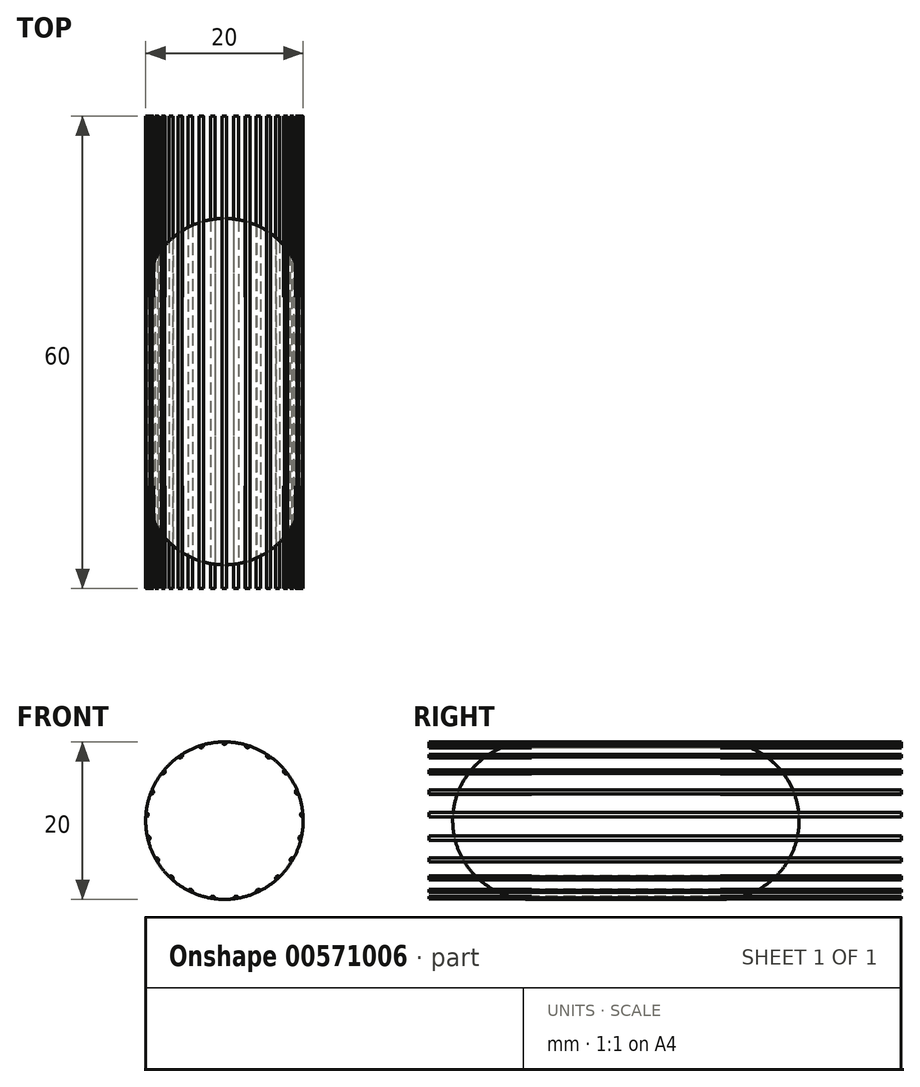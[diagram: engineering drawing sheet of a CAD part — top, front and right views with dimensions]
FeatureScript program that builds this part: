
annotation { "Feature Type Name" : "Feature", "Feature Type Description" : "" }
export const myFeature = defineFeature(function(context is Context, id is Id, definition is map)
    precondition{}
    {
        {
            var Q0;
            Q0=qCreatedBy(makeId("Right.planeOp"),FACE);
            var sketch = newSketch(context, id + "F0", { "sketchPlane" : qUnion([Q0])});
            skPoint(sketch, "E0", {"position": v(-22, 0) * mm});
            skPoint(sketch, "E1", {"position": v(-12, 0) * mm});
            skPoint(sketch, "E2", {"position": v(-12, 10) * mm});
            skEllipse(sketch, "E3", {"center": v(-12, 0) * mm, "majorRadius": 10 * mm, "minorRadius": 10 * mm, "majorAxis": v(-1, 0)});
            skLineSegment(sketch, "E4", {"start": v(-12, 10) * mm, "end": v(0, 10) * mm});
            skLineSegment(sketch, "E5", {"start": v(0, 10) * mm, "end": v(0, 0) * mm});
            skLineSegment(sketch, "E6", {"start": v(0, 0) * mm, "end": v(0, -10) * mm});
            skPoint(sketch, "E6.endSnap0", {"position": v(-12, -10) * mm});
            skLineSegment(sketch, "E7", {"start": v(0, -10) * mm, "end": v(-12, -10) * mm});
            skPoint(sketch, "E8.MirrorP", {"position": v(12, -10) * mm});
            skPoint(sketch, "E9.MirrorP", {"position": v(12, 10) * mm});
            skPoint(sketch, "E10.MirrorP", {"position": v(12, 0) * mm});
            skEllipse(sketch, "E11.MirrorC", {"center": v(12, 0) * mm, "majorRadius": 10 * mm, "minorRadius": 10 * mm, "majorAxis": v(1, 0)});
            skLineSegment(sketch, "E12.MirrorCS", {"start": v(12, 10) * mm, "end": v(0, 10) * mm});
            skPoint(sketch, "E13.MirrorP", {"position": v(22, 0) * mm});
            skLineSegment(sketch, "E14.MirrorCS", {"start": v(0, -10) * mm, "end": v(12, -10) * mm});
            skLineSegment(sketch, "E15", {"start": v(-12, 0) * mm, "end": v(12, 0) * mm});
            skLineSegment(sketch, "E16", {"start": v(-12, 0) * mm, "end": v(-22, 0) * mm});
            skLineSegment(sketch, "E17", {"start": v(12, 0) * mm, "end": v(22, 0) * mm});
            skSolve(sketch);
        }
        {
            var Q0;
            {var subQ4=sQuery(id+"F0.wireOp",EDGE,"E16");Q0=makeQuery(id+"F0.imprint","IMPRINT",FACE,{"disambiguationData":[TD([[makeQuery(id+"F0.imprint","IMPRINT",EDGE,{"derivedFrom":subQ4}),-1.0]])]});}
            var Q1;
            {var subQ0=sQuery(id+"F0.wireOp",EDGE,"E4");Q1=makeQuery(id+"F0.imprint","IMPRINT",FACE,{"disambiguationData":[TD([[makeQuery(id+"F0.imprint","IMPRINT",EDGE,{"derivedFrom":subQ0}),-1.0]])]});}
            var Q2;
            {var subQ0=sQuery(id+"F0.wireOp",EDGE,"E5");Q2=makeQuery(id+"F0.imprint","IMPRINT",FACE,{"disambiguationData":[TD([[makeQuery(id+"F0.imprint","IMPRINT",EDGE,{"derivedFrom":subQ0}),1.0]])]});}
            var Q3;
            {var subQ2=sQuery(id+"F0.wireOp",EDGE,"E17");Q3=makeQuery(id+"F0.imprint","IMPRINT",FACE,{"disambiguationData":[TD([[makeQuery(id+"F0.imprint","IMPRINT",EDGE,{"derivedFrom":subQ2}),1.0]])]});}
            var Q4;
            Q4=sQuery(id+"F0.wireOp",EDGE,"E15");
            revolve(context, id + "F1", {"entities" : qUnion([Q0, Q1, Q2, Q3]), "axis" : qUnion([Q4]), "revolveType" : RevolveType.FULL});
        }
        {
            var Q0;
            Q0=qCreatedBy(makeId("Front.planeOp"),FACE);
            cPlane(context, id + "F2", {"entities" : qUnion([Q0]), "cplaneType" : CPlaneType.OFFSET, "offset" : 25 * mm, "width" : 150 * mm, "height" : 150 * mm});
        }
        {
            var Q0;
            Q0=qCreatedBy(id+"F2.planeOp",FACE);
            var sketch = newSketch(context, id + "F3", { "sketchPlane" : qUnion([Q0])});
            skCircle(sketch, "E18", {"center": v(0, 0) * mm, "radius": 10 * mm, "construction": true});
            skPoint(sketch, "E19", {"position": v(0, 10) * mm});
            skPoint(sketch, "E20", {"position": v(-0.3, 10) * mm});
            skArc(sketch, "E21", {"start": v(-0.3, 10) * mm, "mid": v(0, 9.7) * mm, "end": v(0.3, 10) * mm});
            skArc(sketch, "E22", {"start": v(-0.3, 10) * mm, "mid": v(0, 10) * mm, "end": v(0.3, 10) * mm});
            skSolve(sketch);
        }
        {
            var Q0;
            Q0=makeQuery(id+"F3.imprint","IMPRINT",FACE,{"disambiguationData":[TD([[makeQuery(id+"F3.imprint","IMPRINT",EDGE,{"derivedFrom":sQuery(id+"F3.wireOp",EDGE,"E21")}),1.0]])]});
            extrude(context, id + "F4", {"entities" : qUnion([Q0]), "oppositeDirection" : true, "depth" : 60 * mm, "offsetDistance" : 25 * mm});
        }
        {
            var Q0;
            Q0=makeQuery(id+"F4.opExtrude","SWEPT_BODY",BODY,{"disambiguationData":[OSD([sQuery(id+"F3.wireOp",EDGE,"E21"),sQuery(id+"F3.wireOp",EDGE,"E22")])]});
            var Q1;
            Q1=sQuery(id+"F0.wireOp",EDGE,"E15");
            circularPattern(context, id + "F5", {"entities" : qUnion([Q0]), "axis" : qUnion([Q1]), "angle" : 360 * degree, "instanceCount" : 21, "equalSpace" : true});
        }
    });
